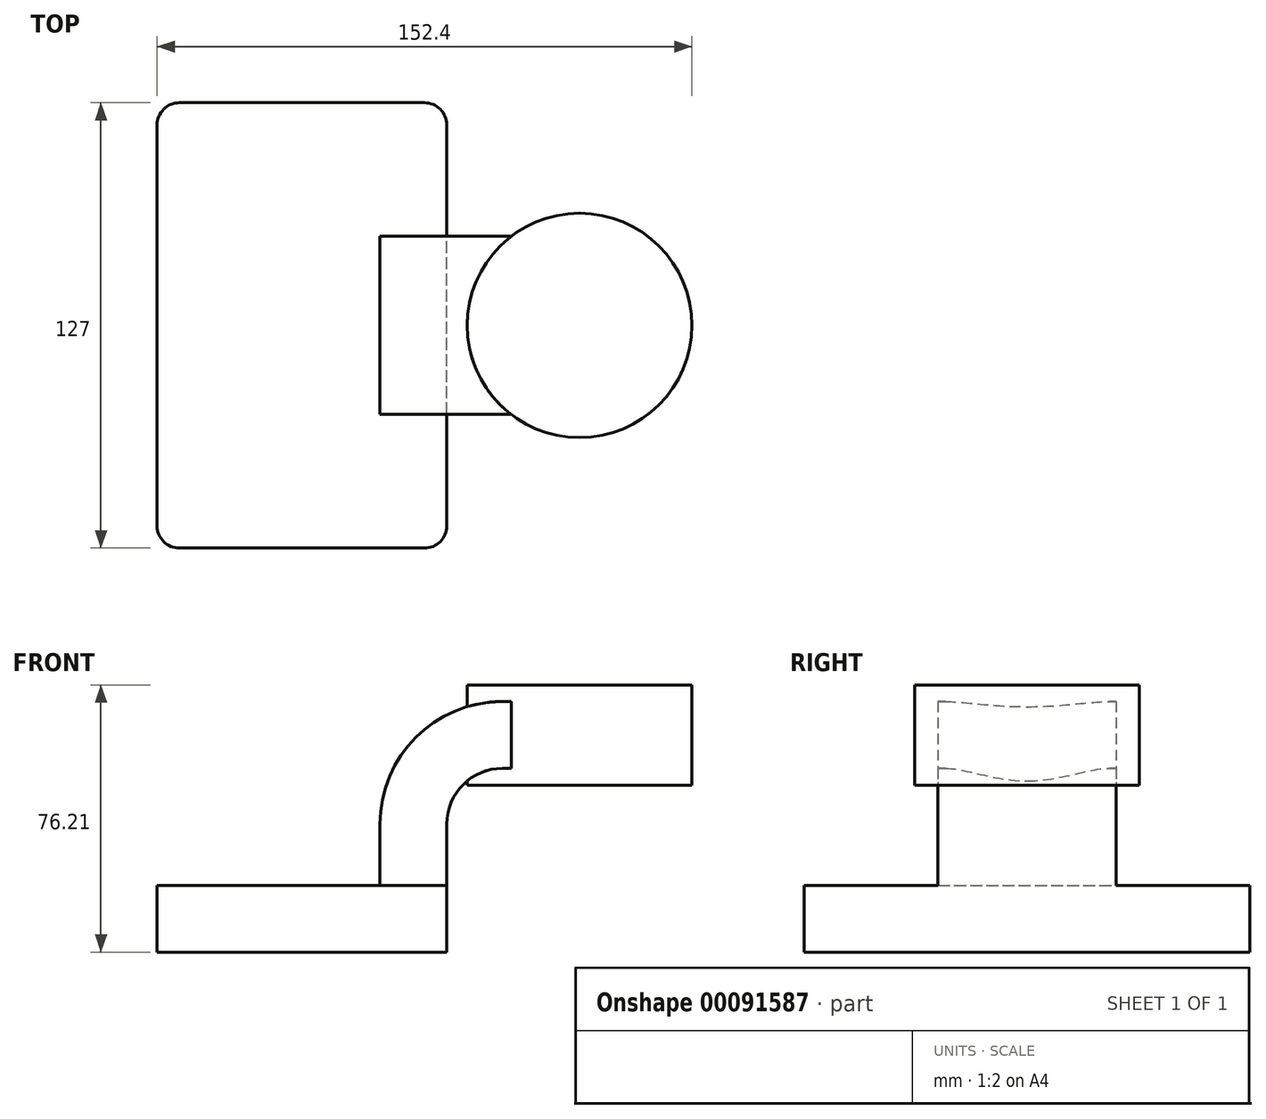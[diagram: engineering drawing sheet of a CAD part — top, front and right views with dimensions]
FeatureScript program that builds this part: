
annotation { "Feature Type Name" : "Feature", "Feature Type Description" : "" }
export const myFeature = defineFeature(function(context is Context, id is Id, definition is map)
    precondition{}
    {
        {
            var Q0;
            Q0=qCreatedBy(makeId("Front.planeOp"),FACE);
            var sketch = newSketch(context, id + "F0", { "sketchPlane" : qUnion([Q0])});
            skLineSegment(sketch, "E0.bottom", {"start": v(41.28, -9.53) * mm, "end": v(-41.28, -9.53) * mm});
            skLineSegment(sketch, "E0.top", {"start": v(41.28, 9.53) * mm, "end": v(-41.28, 9.53) * mm});
            skLineSegment(sketch, "E0.left", {"start": v(41.28, -9.52) * mm, "end": v(41.28, 9.53) * mm});
            skLineSegment(sketch, "E0.right", {"start": v(-41.28, -9.53) * mm, "end": v(-41.28, 9.53) * mm});
            skPoint(sketch, "E0.middle", {"position": v(0, 0) * mm});
            skLineSegment(sketch, "E1.bottom", {"start": v(111.12, 38.1) * mm, "end": v(60.33, 38.1) * mm});
            skLineSegment(sketch, "E1.top", {"start": v(111.12, 66.68) * mm, "end": v(60.33, 66.68) * mm});
            skLineSegment(sketch, "E1.left", {"start": v(111.13, 38.1) * mm, "end": v(111.13, 66.68) * mm});
            skLineSegment(sketch, "E1.right", {"start": v(60.33, 38.1) * mm, "end": v(60.33, 66.68) * mm});
            skPoint(sketch, "E1.middle", {"position": v(85.72, 52.39) * mm});
            skLineSegment(sketch, "E2", {"start": v(41.28, 9.53) * mm, "end": v(41.28, 27) * mm});
            skArc(sketch, "E3", {"start": v(41.27, 27) * mm, "mid": v(45.92, 38.23) * mm, "end": v(57.15, 42.88) * mm});
            skLineSegment(sketch, "E4", {"start": v(57.15, 42.88) * mm, "end": v(79.12, 42.88) * mm});
            skLineSegment(sketch, "E5.0", {"start": v(57.15, 61.93) * mm, "end": v(79.12, 61.93) * mm});
            skArc(sketch, "E5.1", {"start": v(22.23, 27) * mm, "mid": v(32.45, 51.7) * mm, "end": v(57.15, 61.93) * mm});
            skLineSegment(sketch, "E5.2", {"start": v(22.23, 8.75) * mm, "end": v(22.23, 27) * mm});
            skLineSegment(sketch, "E6", {"start": v(79.12, 38.1) * mm, "end": v(79.12, 66.68) * mm});
            skFitSpline(sketch, "E7", {"points": [v(-41.28, 9.53) * mm, v(60.33, 66.68) * mm], "startDerivative": vector(-6.63, 94.96) * mm, "endDerivative": vector(129.66, 37.16) * mm});
            skSolve(sketch);
        }
        {
            var Q0;
            Q0=makeQuery(id+"F0.imprint","IMPRINT",FACE,{"disambiguationData":[TD([[makeQuery(id+"F0.imprint","IMPRINT",EDGE,{"derivedFrom":sQuery(id+"F0.wireOp",EDGE,"E0.bottom")}),-1.0]])]});
            extrude(context, id + "F1", {"entities" : qUnion([Q0]), "endBound" : BoundingType.SYMMETRIC, "depth" : 127 * mm});
        }
        {
            var Q0;
            {var subQ1=sQuery(id+"F0.wireOp",EDGE,"E2");Q0=makeQuery(id+"F0.imprint","IMPRINT",FACE,{"disambiguationData":[TD([[makeQuery(id+"F0.imprint","IMPRINT",EDGE,{"derivedFrom":subQ1}),1.0]])]});}
            extrude(context, id + "F2", {"entities" : qUnion([Q0]), "operationType" : NewBodyOperationType.ADD, "endBound" : BoundingType.SYMMETRIC, "depth" : 50.8 * mm});
        }
        {
            var Q0;
            {var subQ0=sQuery(id+"F0.wireOp",EDGE,"E5.1");Q0=makeQuery(id+"F0.imprint","IMPRINT",FACE,{"disambiguationData":[TD([[makeQuery(id+"F0.imprint","IMPRINT",EDGE,{"derivedFrom":subQ0}),1.0]])]});}
            extrude(context, id + "F3", {"entities" : qUnion([Q0]), "operationType" : NewBodyOperationType.ADD, "endBound" : BoundingType.SYMMETRIC, "depth" : 15.88 * mm});
        }
        {
            var Q0;
            {var subQ0=sQuery(id+"F0.wireOp",EDGE,"E1.left");Q0=makeQuery(id+"F0.imprint","IMPRINT",FACE,{"disambiguationData":[TD([[makeQuery(id+"F0.imprint","IMPRINT",EDGE,{"derivedFrom":subQ0}),1.0]])]});}
            var Q1;
            Q1=sQuery(id+"F0.wireOp",EDGE,"E6");
            revolve(context, id + "F4", {"operationType" : NewBodyOperationType.ADD, "entities" : qUnion([Q0]), "axis" : qUnion([Q1]), "revolveType" : RevolveType.FULL});
        }
        {
            var Q0;
            Q0=makeQuery(id+"F1.opExtrude","CAP_EDGE",EDGE,{"disambiguationData":[OSD([sQuery(id+"F0.wireOp",EDGE,"E0.left")])],"isStart":false});
            var Q1;
            Q1=makeQuery(id+"F1.opExtrude","CAP_EDGE",EDGE,{"disambiguationData":[OSD([sQuery(id+"F0.wireOp",EDGE,"E0.right")])],"isStart":false});
            var Q2;
            Q2=makeQuery(id+"F1.opExtrude","CAP_EDGE",EDGE,{"disambiguationData":[OSD([sQuery(id+"F0.wireOp",EDGE,"E0.right")])],"isStart":true});
            var Q3;
            Q3=makeQuery(id+"F1.opExtrude","CAP_EDGE",EDGE,{"disambiguationData":[OSD([sQuery(id+"F0.wireOp",EDGE,"E0.left")])],"isStart":true});
            fillet(context, id + "F5", {"entities" : qUnion([Q0, Q1, Q2, Q3]), "radius" : 6.35 * mm, "tangentPropagation" : true, "allowEdgeOverflow" : false});
        }
    });
